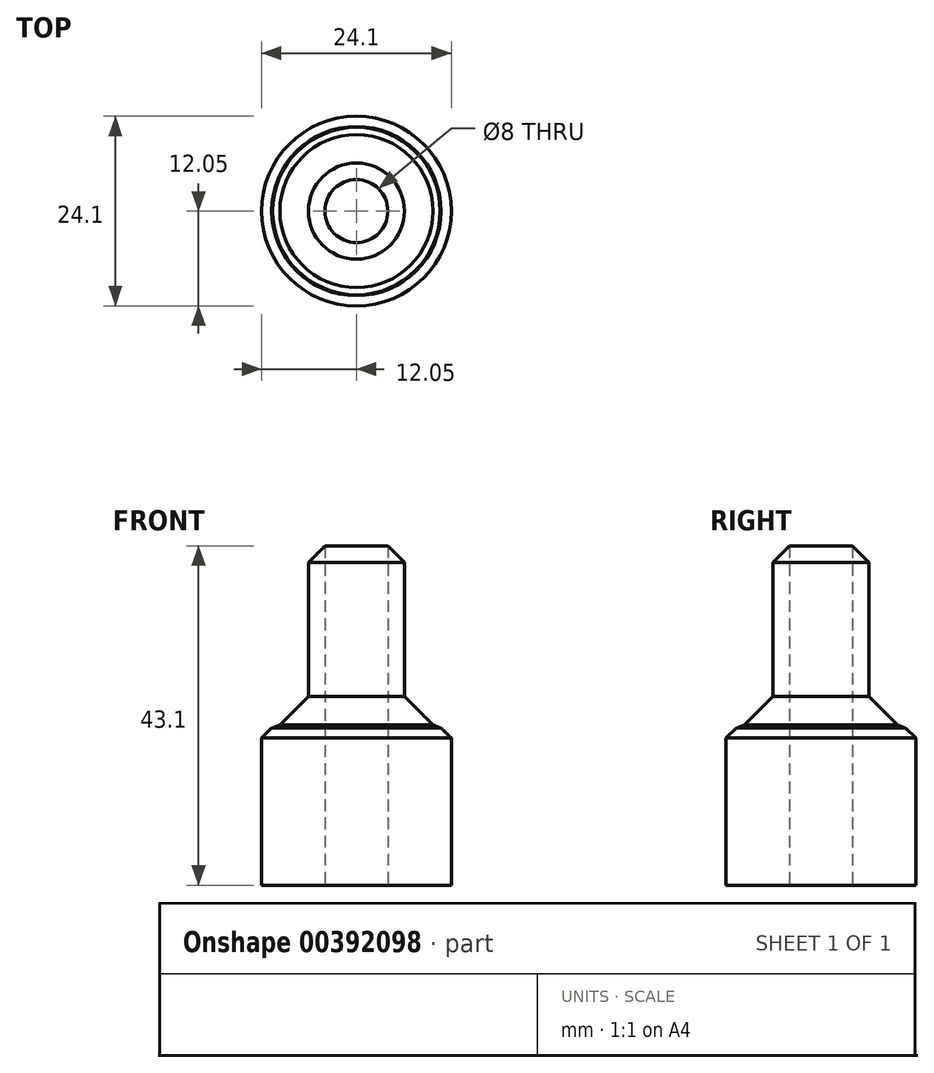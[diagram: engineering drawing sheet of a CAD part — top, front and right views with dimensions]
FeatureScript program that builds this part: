
annotation { "Feature Type Name" : "Feature", "Feature Type Description" : "" }
export const myFeature = defineFeature(function(context is Context, id is Id, definition is map)
    precondition{}
    {
        {
            var Q0;
            Q0=qCreatedBy(makeId("Top.planeOp"),FACE);
            var sketch = newSketch(context, id + "F0", { "sketchPlane" : qUnion([Q0])});
            skCircle(sketch, "E0", {"center": v(0, 0) * mm, "radius": 12.05 * mm});
            skCircle(sketch, "E1", {"center": v(0, 0) * mm, "radius": 4 * mm});
            skSolve(sketch);
        }
        {
            var Q0;
            Q0 = qSketchRegion(id + "F0", true);
            extrude(context, id + "F1", {"entities" : qUnion([Q0]), "depth" : 45 * mm});
        }
        {
            var Q0;
            Q0=makeQuery(id+"F1.opExtrude","CAP_FACE",FACE,{"disambiguationData":[OSD([sQuery(id+"F0.wireOp",EDGE,"E0"),sQuery(id+"F0.wireOp",EDGE,"E1")])],"isStart":false});
            var sketch = newSketch(context, id + "F2", { "sketchPlane" : qUnion([Q0])});
            skCircle(sketch, "E2", {"center": v(0, 0) * mm, "radius": 6.1 * mm});
            skCircle(sketch, "E3", {"center": v(0, 0) * mm, "radius": 13.77 * mm});
            skSolve(sketch);
        }
        {
            var Q0;
            Q0 = qSketchRegion(id + "F2", true);
            extrude(context, id + "F3", {"entities" : qUnion([Q0]), "operationType" : NewBodyOperationType.REMOVE, "oppositeDirection" : true, "depth" : 25 * mm});
        }
        {
            var Q0;
            Q0=makeQuery(id+"F3.boolean.opBoolean","COPY",FACE,{"derivedFrom":makeQuery(id+"F3.opExtrude","SWEPT_FACE",FACE,{"disambiguationData":[OSD([sQuery(id+"F2.wireOp",EDGE,"E2")])]})});
            chamfer(context, id + "F4", {"entities" : qUnion([Q0]), "width" : 4 * mm, "tangentPropagation" : true});
        }
        {
            var Q0;
            Q0=makeQuery(id+"F3.boolean.opBoolean","COPY",FACE,{"derivedFrom":makeQuery(id+"F3.opExtrude","CAP_FACE",FACE,{"disambiguationData":[OSD([sQuery(id+"F2.wireOp",EDGE,"E2"),sQuery(id+"F2.wireOp",EDGE,"E3")])],"isStart":false})});
            chamfer(context, id + "F5", {"entities" : qUnion([Q0]), "width" : 1.3 * mm, "tangentPropagation" : true});
        }
    });
